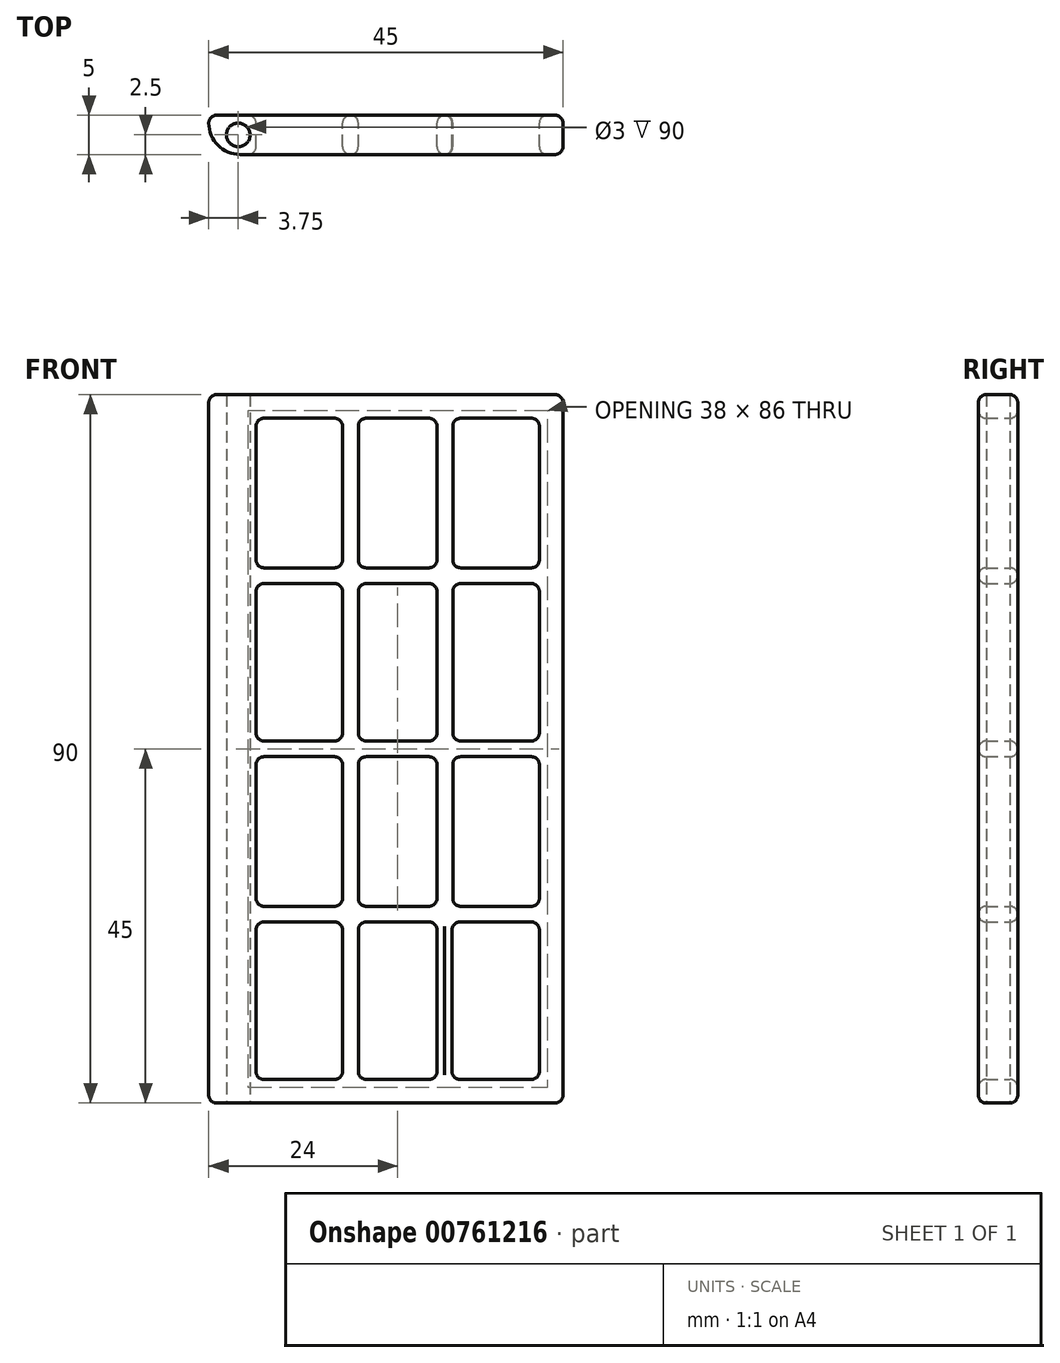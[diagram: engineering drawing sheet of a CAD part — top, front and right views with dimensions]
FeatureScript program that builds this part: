
annotation { "Feature Type Name" : "Feature", "Feature Type Description" : "" }
export const myFeature = defineFeature(function(context is Context, id is Id, definition is map)
    precondition{}
    {
        {
            var Q0;
            Q0=qCreatedBy(makeId("Front.planeOp"),FACE);
            var sketch = newSketch(context, id + "F0", { "sketchPlane" : qUnion([Q0])});
            skLineSegment(sketch, "E0.bottom", {"start": v(0, 0) * mm, "end": v(45, 0) * mm});
            skLineSegment(sketch, "E0.top", {"start": v(0, 90) * mm, "end": v(45, 90) * mm});
            skLineSegment(sketch, "E0.left", {"start": v(0, 0) * mm, "end": v(0, 90) * mm});
            skLineSegment(sketch, "E0.right", {"start": v(45, 0) * mm, "end": v(45, 90) * mm});
            skLineSegment(sketch, "E1.bottom", {"start": v(6, 87) * mm, "end": v(17, 87) * mm});
            skLineSegment(sketch, "E1.top", {"start": v(6, 68) * mm, "end": v(17, 68) * mm});
            skLineSegment(sketch, "E1.left", {"start": v(6, 87) * mm, "end": v(6, 68) * mm});
            skLineSegment(sketch, "E1.right", {"start": v(17, 87) * mm, "end": v(17, 68) * mm});
            skLineSegment(sketch, "E2.bottom", {"start": v(19, 87) * mm, "end": v(29, 87) * mm});
            skLineSegment(sketch, "E2.top", {"start": v(19, 68) * mm, "end": v(29, 68) * mm});
            skLineSegment(sketch, "E2.left", {"start": v(19, 87) * mm, "end": v(19, 68) * mm});
            skLineSegment(sketch, "E2.right", {"start": v(29, 87) * mm, "end": v(29, 68) * mm});
            skLineSegment(sketch, "E3.bottom", {"start": v(31, 87) * mm, "end": v(42, 87) * mm});
            skLineSegment(sketch, "E3.top", {"start": v(31, 68) * mm, "end": v(42, 68) * mm});
            skLineSegment(sketch, "E3.left", {"start": v(31, 87) * mm, "end": v(31, 68) * mm});
            skLineSegment(sketch, "E3.right", {"start": v(42, 87) * mm, "end": v(42, 68) * mm});
            skLineSegment(sketch, "E4.bottom", {"start": v(6, 66) * mm, "end": v(17, 66) * mm});
            skLineSegment(sketch, "E4.top", {"start": v(6, 46) * mm, "end": v(17, 46) * mm});
            skLineSegment(sketch, "E4.left", {"start": v(6, 66) * mm, "end": v(6, 46) * mm});
            skLineSegment(sketch, "E4.right", {"start": v(17, 66) * mm, "end": v(17, 46) * mm});
            skLineSegment(sketch, "E5.bottom", {"start": v(19, 66) * mm, "end": v(29, 66) * mm});
            skLineSegment(sketch, "E5.top", {"start": v(19, 46) * mm, "end": v(29, 46) * mm});
            skLineSegment(sketch, "E5.left", {"start": v(19, 66) * mm, "end": v(19, 46) * mm});
            skLineSegment(sketch, "E5.right", {"start": v(29, 66) * mm, "end": v(29, 46) * mm});
            skLineSegment(sketch, "E6.bottom", {"start": v(31, 66) * mm, "end": v(42, 66) * mm});
            skLineSegment(sketch, "E6.top", {"start": v(31, 46) * mm, "end": v(42, 46) * mm});
            skLineSegment(sketch, "E6.left", {"start": v(31, 66) * mm, "end": v(31, 46) * mm});
            skLineSegment(sketch, "E6.right", {"start": v(42, 66) * mm, "end": v(42, 46) * mm});
            skLineSegment(sketch, "E7.bottom", {"start": v(6, 44) * mm, "end": v(17, 44) * mm});
            skLineSegment(sketch, "E7.top", {"start": v(6, 25) * mm, "end": v(17, 25) * mm});
            skLineSegment(sketch, "E7.left", {"start": v(6, 44) * mm, "end": v(6, 25) * mm});
            skLineSegment(sketch, "E7.right", {"start": v(17, 44) * mm, "end": v(17, 25) * mm});
            skLineSegment(sketch, "E8.bottom", {"start": v(19, 44) * mm, "end": v(29, 44) * mm});
            skLineSegment(sketch, "E8.top", {"start": v(19, 25) * mm, "end": v(29, 25) * mm});
            skLineSegment(sketch, "E8.left", {"start": v(19, 44) * mm, "end": v(19, 25) * mm});
            skLineSegment(sketch, "E8.right", {"start": v(29, 44) * mm, "end": v(29, 25) * mm});
            skLineSegment(sketch, "E9.bottom", {"start": v(31, 44) * mm, "end": v(42, 44) * mm});
            skLineSegment(sketch, "E9.top", {"start": v(31, 25) * mm, "end": v(42, 25) * mm});
            skLineSegment(sketch, "E9.left", {"start": v(31, 44) * mm, "end": v(31, 25) * mm});
            skLineSegment(sketch, "E9.right", {"start": v(42, 44) * mm, "end": v(42, 25) * mm});
            skLineSegment(sketch, "E10.bottom", {"start": v(6, 23) * mm, "end": v(17, 23) * mm});
            skLineSegment(sketch, "E10.top", {"start": v(6, 3) * mm, "end": v(17, 3) * mm});
            skLineSegment(sketch, "E10.left", {"start": v(6, 23) * mm, "end": v(6, 3) * mm});
            skLineSegment(sketch, "E10.right", {"start": v(17, 23) * mm, "end": v(17, 3) * mm});
            skLineSegment(sketch, "E11.bottom", {"start": v(19, 23) * mm, "end": v(29, 23) * mm});
            skLineSegment(sketch, "E11.top", {"start": v(19, 3) * mm, "end": v(29, 3) * mm});
            skLineSegment(sketch, "E11.left", {"start": v(19, 23) * mm, "end": v(19, 3) * mm});
            skLineSegment(sketch, "E11.right", {"start": v(29, 23) * mm, "end": v(29, 3) * mm});
            skLineSegment(sketch, "E12.bottom", {"start": v(30.9, 23) * mm, "end": v(42, 23) * mm});
            skLineSegment(sketch, "E12.left", {"start": v(30.9, 23) * mm, "end": v(30.9, 3) * mm});
            skLineSegment(sketch, "E12.right", {"start": v(42, 23) * mm, "end": v(42, 3) * mm});
            skLineSegment(sketch, "E13", {"start": v(30.9, 3) * mm, "end": v(42, 3) * mm});
            skSolve(sketch);
        }
        {
            var Q0;
            Q0=makeQuery(id+"F0.imprint","IMPRINT",FACE,{"disambiguationData":[TD([[makeQuery(id+"F0.imprint","IMPRINT",EDGE,{"derivedFrom":sQuery(id+"F0.wireOp",EDGE,"E0.bottom")}),1.0]])]});
            extrude(context, id + "F1", {"entities" : qUnion([Q0]), "depth" : 5 * mm, "offsetDistance" : 25 * mm});
        }
        {
            var Q0;
            Q0=qCreatedBy(makeId("Top.planeOp"),FACE);
            var sketch = newSketch(context, id + "F2", { "sketchPlane" : qUnion([Q0])});
            skPoint(sketch, "E14", {"position": v(3.75, -2.5) * mm});
            skSolve(sketch);
        }
        {
            var Q0;
            Q0=sQuery(id+"F2.wireOp",VERTEX,"E14");
            var Q1;
            Q1=makeQuery(id+"F1.opExtrude","SWEPT_BODY",BODY,{"disambiguationData":[OSD([sQuery(id+"F0.wireOp",EDGE,"E0.bottom"),sQuery(id+"F0.wireOp",EDGE,"E0.top"),sQuery(id+"F0.wireOp",EDGE,"E0.left"),sQuery(id+"F0.wireOp",EDGE,"E0.right"),sQuery(id+"F0.wireOp",EDGE,"E1.bottom"),sQuery(id+"F0.wireOp",EDGE,"E1.top"),sQuery(id+"F0.wireOp",EDGE,"E1.left"),sQuery(id+"F0.wireOp",EDGE,"E1.right"),sQuery(id+"F0.wireOp",EDGE,"E2.bottom"),sQuery(id+"F0.wireOp",EDGE,"E2.top"),sQuery(id+"F0.wireOp",EDGE,"E2.left"),sQuery(id+"F0.wireOp",EDGE,"E2.right"),sQuery(id+"F0.wireOp",EDGE,"E3.bottom"),sQuery(id+"F0.wireOp",EDGE,"E3.top"),sQuery(id+"F0.wireOp",EDGE,"E3.left"),sQuery(id+"F0.wireOp",EDGE,"E3.right"),sQuery(id+"F0.wireOp",EDGE,"E4.bottom"),sQuery(id+"F0.wireOp",EDGE,"E4.top"),sQuery(id+"F0.wireOp",EDGE,"E4.left"),sQuery(id+"F0.wireOp",EDGE,"E4.right"),sQuery(id+"F0.wireOp",EDGE,"E5.bottom"),sQuery(id+"F0.wireOp",EDGE,"E5.top"),sQuery(id+"F0.wireOp",EDGE,"E5.left"),sQuery(id+"F0.wireOp",EDGE,"E5.right"),sQuery(id+"F0.wireOp",EDGE,"E6.bottom"),sQuery(id+"F0.wireOp",EDGE,"E6.top"),sQuery(id+"F0.wireOp",EDGE,"E6.left"),sQuery(id+"F0.wireOp",EDGE,"E6.right"),sQuery(id+"F0.wireOp",EDGE,"E7.bottom"),sQuery(id+"F0.wireOp",EDGE,"E7.top"),sQuery(id+"F0.wireOp",EDGE,"E7.left"),sQuery(id+"F0.wireOp",EDGE,"E7.right"),sQuery(id+"F0.wireOp",EDGE,"E8.bottom"),sQuery(id+"F0.wireOp",EDGE,"E8.top"),sQuery(id+"F0.wireOp",EDGE,"E8.left"),sQuery(id+"F0.wireOp",EDGE,"E8.right"),sQuery(id+"F0.wireOp",EDGE,"E9.bottom"),sQuery(id+"F0.wireOp",EDGE,"E9.top"),sQuery(id+"F0.wireOp",EDGE,"E9.left"),sQuery(id+"F0.wireOp",EDGE,"E9.right"),sQuery(id+"F0.wireOp",EDGE,"E10.bottom"),sQuery(id+"F0.wireOp",EDGE,"E10.top"),sQuery(id+"F0.wireOp",EDGE,"E10.left"),sQuery(id+"F0.wireOp",EDGE,"E10.right"),sQuery(id+"F0.wireOp",EDGE,"E11.bottom"),sQuery(id+"F0.wireOp",EDGE,"E11.top"),sQuery(id+"F0.wireOp",EDGE,"E11.left"),sQuery(id+"F0.wireOp",EDGE,"E11.right"),sQuery(id+"F0.wireOp",EDGE,"E12.bottom"),sQuery(id+"F0.wireOp",EDGE,"E12.left"),sQuery(id+"F0.wireOp",EDGE,"E12.right"),sQuery(id+"F0.wireOp",EDGE,"E13")])]});
            hole(context, id + "F3", {"style" : HoleStyle.SIMPLE, "endStyle" : HoleEndStyle.BLIND, "oppositeDirection" : true, "holeDiameter" : 3 * mm, "majorDiameter" : 5 * mm, "holeDepth" : 150 * mm, "isTappedThrough" : true, "tappedDepth" : 12 * mm, "tapClearance" : 3, "locations" : qUnion([Q0]), "scope" : qUnion([Q1])});
        }
        {
            var Q0;
            Q0=makeQuery(id+"F1.opExtrude","CAP_EDGE",EDGE,{"disambiguationData":[OSD([sQuery(id+"F0.wireOp",EDGE,"E0.left")])],"isStart":false});
            fillet(context, id + "F4", {"entities" : qUnion([Q0]), "radius" : 4 * mm, "tangentPropagation" : true, "allowEdgeOverflow" : false});
        }
        {
            var Q0;
            Q0=makeQuery(id+"F1.opExtrude","CAP_EDGE",EDGE,{"disambiguationData":[OSD([sQuery(id+"F0.wireOp",EDGE,"E1.left")])],"isStart":false});
            var Q1;
            Q1=makeQuery(id+"F1.opExtrude","CAP_EDGE",EDGE,{"disambiguationData":[OSD([sQuery(id+"F0.wireOp",EDGE,"E1.bottom")])],"isStart":false});
            var Q2;
            Q2=makeQuery(id+"F1.opExtrude","CAP_EDGE",EDGE,{"disambiguationData":[OSD([sQuery(id+"F0.wireOp",EDGE,"E1.right")])],"isStart":false});
            var Q3;
            Q3=makeQuery(id+"F1.opExtrude","CAP_EDGE",EDGE,{"disambiguationData":[OSD([sQuery(id+"F0.wireOp",EDGE,"E1.top")])],"isStart":false});
            var Q4;
            Q4=makeQuery(id+"F1.opExtrude","CAP_EDGE",EDGE,{"disambiguationData":[OSD([sQuery(id+"F0.wireOp",EDGE,"E2.left")])],"isStart":false});
            var Q5;
            Q5=makeQuery(id+"F1.opExtrude","CAP_EDGE",EDGE,{"disambiguationData":[OSD([sQuery(id+"F0.wireOp",EDGE,"E2.bottom")])],"isStart":false});
            var Q6;
            Q6=makeQuery(id+"F1.opExtrude","CAP_EDGE",EDGE,{"disambiguationData":[OSD([sQuery(id+"F0.wireOp",EDGE,"E2.right")])],"isStart":false});
            var Q7;
            Q7=makeQuery(id+"F1.opExtrude","CAP_EDGE",EDGE,{"disambiguationData":[OSD([sQuery(id+"F0.wireOp",EDGE,"E2.top")])],"isStart":false});
            var Q8;
            Q8=makeQuery(id+"F1.opExtrude","CAP_EDGE",EDGE,{"disambiguationData":[OSD([sQuery(id+"F0.wireOp",EDGE,"E3.left")])],"isStart":false});
            var Q9;
            Q9=makeQuery(id+"F1.opExtrude","CAP_EDGE",EDGE,{"disambiguationData":[OSD([sQuery(id+"F0.wireOp",EDGE,"E3.bottom")])],"isStart":false});
            var Q10;
            Q10=makeQuery(id+"F1.opExtrude","CAP_EDGE",EDGE,{"disambiguationData":[OSD([sQuery(id+"F0.wireOp",EDGE,"E3.right")])],"isStart":false});
            var Q11;
            Q11=makeQuery(id+"F1.opExtrude","CAP_EDGE",EDGE,{"disambiguationData":[OSD([sQuery(id+"F0.wireOp",EDGE,"E3.top")])],"isStart":false});
            var Q12;
            Q12=makeQuery(id+"F1.opExtrude","CAP_EDGE",EDGE,{"disambiguationData":[OSD([sQuery(id+"F0.wireOp",EDGE,"E4.left")])],"isStart":false});
            var Q13;
            Q13=makeQuery(id+"F1.opExtrude","CAP_EDGE",EDGE,{"disambiguationData":[OSD([sQuery(id+"F0.wireOp",EDGE,"E4.bottom")])],"isStart":false});
            var Q14;
            Q14=makeQuery(id+"F1.opExtrude","CAP_EDGE",EDGE,{"disambiguationData":[OSD([sQuery(id+"F0.wireOp",EDGE,"E4.right")])],"isStart":false});
            var Q15;
            Q15=makeQuery(id+"F1.opExtrude","CAP_EDGE",EDGE,{"disambiguationData":[OSD([sQuery(id+"F0.wireOp",EDGE,"E13")])],"isStart":false});
            var Q16;
            Q16=makeQuery(id+"F1.opExtrude","CAP_EDGE",EDGE,{"disambiguationData":[OSD([sQuery(id+"F0.wireOp",EDGE,"E0.bottom")])],"isStart":false});
            var Q17;
            Q17=makeQuery(id+"F1.opExtrude","CAP_EDGE",EDGE,{"disambiguationData":[OSD([sQuery(id+"F0.wireOp",EDGE,"E12.bottom")])],"isStart":false});
            var Q18;
            Q18=makeQuery(id+"F1.opExtrude","CAP_EDGE",EDGE,{"disambiguationData":[OSD([sQuery(id+"F0.wireOp",EDGE,"E8.top")])],"isStart":false});
            var Q19;
            Q19=makeQuery(id+"F1.opExtrude","CAP_EDGE",EDGE,{"disambiguationData":[OSD([sQuery(id+"F0.wireOp",EDGE,"E4.top")])],"isStart":false});
            var Q20;
            Q20=makeQuery(id+"F1.opExtrude","CAP_EDGE",EDGE,{"disambiguationData":[OSD([sQuery(id+"F0.wireOp",EDGE,"E12.right")])],"isStart":false});
            var Q21;
            Q21=makeQuery(id+"F1.opExtrude","CAP_EDGE",EDGE,{"disambiguationData":[OSD([sQuery(id+"F0.wireOp",EDGE,"E6.right")])],"isStart":false});
            var Q22;
            Q22=makeQuery(id+"F1.opExtrude","CAP_EDGE",EDGE,{"disambiguationData":[OSD([sQuery(id+"F0.wireOp",EDGE,"E8.right")])],"isStart":false});
            var Q23;
            Q23=makeQuery(id+"F1.opExtrude","CAP_EDGE",EDGE,{"disambiguationData":[OSD([sQuery(id+"F0.wireOp",EDGE,"E10.left")])],"isStart":false});
            var Q24;
            Q24=makeQuery(id+"F1.opExtrude","CAP_EDGE",EDGE,{"disambiguationData":[OSD([sQuery(id+"F0.wireOp",EDGE,"E6.left")])],"isStart":false});
            var Q25;
            Q25=makeQuery(id+"F1.opExtrude","CAP_EDGE",EDGE,{"disambiguationData":[OSD([sQuery(id+"F0.wireOp",EDGE,"E8.bottom")])],"isStart":false});
            var Q26;
            Q26=makeQuery(id+"F1.opExtrude","CAP_EDGE",EDGE,{"disambiguationData":[OSD([sQuery(id+"F0.wireOp",EDGE,"E0.right")])],"isStart":true});
            var Q27;
            Q27=makeQuery(id+"F1.opExtrude","CAP_EDGE",EDGE,{"disambiguationData":[OSD([sQuery(id+"F0.wireOp",EDGE,"E0.top")])],"isStart":true});
            var Q28;
            Q28=makeQuery(id+"F1.opExtrude","CAP_EDGE",EDGE,{"disambiguationData":[OSD([sQuery(id+"F0.wireOp",EDGE,"E6.bottom")])],"isStart":false});
            var Q29;
            Q29=makeQuery(id+"F1.opExtrude","CAP_EDGE",EDGE,{"disambiguationData":[OSD([sQuery(id+"F0.wireOp",EDGE,"E10.right")])],"isStart":false});
            var Q30;
            Q30=makeQuery(id+"F1.opExtrude","CAP_EDGE",EDGE,{"disambiguationData":[OSD([sQuery(id+"F0.wireOp",EDGE,"E10.top")])],"isStart":false});
            var Q31;
            {var subQ0=sQuery(id+"F0.wireOp",EDGE,"E0.left");Q31=makeQuery(id+"F4.opFillet","BLEND_EDGE",EDGE,{"blendedFrom":[makeQuery(id+"F1.opExtrude","CAP_EDGE",EDGE,{"disambiguationData":[OSD([subQ0])],"isStart":false}),makeQuery(id+"F1.opExtrude","CAP_FACE",FACE,{"disambiguationData":[OSD([sQuery(id+"F0.wireOp",EDGE,"E0.bottom"),sQuery(id+"F0.wireOp",EDGE,"E0.top"),subQ0,sQuery(id+"F0.wireOp",EDGE,"E0.right"),sQuery(id+"F0.wireOp",EDGE,"E1.bottom"),sQuery(id+"F0.wireOp",EDGE,"E1.top"),sQuery(id+"F0.wireOp",EDGE,"E1.left"),sQuery(id+"F0.wireOp",EDGE,"E1.right"),sQuery(id+"F0.wireOp",EDGE,"E2.bottom"),sQuery(id+"F0.wireOp",EDGE,"E2.top"),sQuery(id+"F0.wireOp",EDGE,"E2.left"),sQuery(id+"F0.wireOp",EDGE,"E2.right"),sQuery(id+"F0.wireOp",EDGE,"E3.bottom"),sQuery(id+"F0.wireOp",EDGE,"E3.top"),sQuery(id+"F0.wireOp",EDGE,"E3.left"),sQuery(id+"F0.wireOp",EDGE,"E3.right"),sQuery(id+"F0.wireOp",EDGE,"E4.bottom"),sQuery(id+"F0.wireOp",EDGE,"E4.top"),sQuery(id+"F0.wireOp",EDGE,"E4.left"),sQuery(id+"F0.wireOp",EDGE,"E4.right"),sQuery(id+"F0.wireOp",EDGE,"E5.bottom"),sQuery(id+"F0.wireOp",EDGE,"E5.top"),sQuery(id+"F0.wireOp",EDGE,"E5.left"),sQuery(id+"F0.wireOp",EDGE,"E5.right"),sQuery(id+"F0.wireOp",EDGE,"E6.bottom"),sQuery(id+"F0.wireOp",EDGE,"E6.top"),sQuery(id+"F0.wireOp",EDGE,"E6.left"),sQuery(id+"F0.wireOp",EDGE,"E6.right"),sQuery(id+"F0.wireOp",EDGE,"E7.bottom"),sQuery(id+"F0.wireOp",EDGE,"E7.top"),sQuery(id+"F0.wireOp",EDGE,"E7.left"),sQuery(id+"F0.wireOp",EDGE,"E7.right"),sQuery(id+"F0.wireOp",EDGE,"E8.bottom"),sQuery(id+"F0.wireOp",EDGE,"E8.top"),sQuery(id+"F0.wireOp",EDGE,"E8.left"),sQuery(id+"F0.wireOp",EDGE,"E8.right"),sQuery(id+"F0.wireOp",EDGE,"E9.bottom"),sQuery(id+"F0.wireOp",EDGE,"E9.top"),sQuery(id+"F0.wireOp",EDGE,"E9.left"),sQuery(id+"F0.wireOp",EDGE,"E9.right"),sQuery(id+"F0.wireOp",EDGE,"E10.bottom"),sQuery(id+"F0.wireOp",EDGE,"E10.top"),sQuery(id+"F0.wireOp",EDGE,"E10.left"),sQuery(id+"F0.wireOp",EDGE,"E10.right"),sQuery(id+"F0.wireOp",EDGE,"E11.bottom"),sQuery(id+"F0.wireOp",EDGE,"E11.top"),sQuery(id+"F0.wireOp",EDGE,"E11.left"),sQuery(id+"F0.wireOp",EDGE,"E11.right"),sQuery(id+"F0.wireOp",EDGE,"E12.bottom"),sQuery(id+"F0.wireOp",EDGE,"E12.left"),sQuery(id+"F0.wireOp",EDGE,"E12.right"),sQuery(id+"F0.wireOp",EDGE,"E13")])],"isStart":false})],"blendedInto":[makeQuery(id+"F1.opExtrude","CAP_FACE",FACE,{"disambiguationData":[OSD([sQuery(id+"F0.wireOp",EDGE,"E0.bottom"),sQuery(id+"F0.wireOp",EDGE,"E0.top"),subQ0,sQuery(id+"F0.wireOp",EDGE,"E0.right"),sQuery(id+"F0.wireOp",EDGE,"E1.bottom"),sQuery(id+"F0.wireOp",EDGE,"E1.top"),sQuery(id+"F0.wireOp",EDGE,"E1.left"),sQuery(id+"F0.wireOp",EDGE,"E1.right"),sQuery(id+"F0.wireOp",EDGE,"E2.bottom"),sQuery(id+"F0.wireOp",EDGE,"E2.top"),sQuery(id+"F0.wireOp",EDGE,"E2.left"),sQuery(id+"F0.wireOp",EDGE,"E2.right"),sQuery(id+"F0.wireOp",EDGE,"E3.bottom"),sQuery(id+"F0.wireOp",EDGE,"E3.top"),sQuery(id+"F0.wireOp",EDGE,"E3.left"),sQuery(id+"F0.wireOp",EDGE,"E3.right"),sQuery(id+"F0.wireOp",EDGE,"E4.bottom"),sQuery(id+"F0.wireOp",EDGE,"E4.top"),sQuery(id+"F0.wireOp",EDGE,"E4.left"),sQuery(id+"F0.wireOp",EDGE,"E4.right"),sQuery(id+"F0.wireOp",EDGE,"E5.bottom"),sQuery(id+"F0.wireOp",EDGE,"E5.top"),sQuery(id+"F0.wireOp",EDGE,"E5.left"),sQuery(id+"F0.wireOp",EDGE,"E5.right"),sQuery(id+"F0.wireOp",EDGE,"E6.bottom"),sQuery(id+"F0.wireOp",EDGE,"E6.top"),sQuery(id+"F0.wireOp",EDGE,"E6.left"),sQuery(id+"F0.wireOp",EDGE,"E6.right"),sQuery(id+"F0.wireOp",EDGE,"E7.bottom"),sQuery(id+"F0.wireOp",EDGE,"E7.top"),sQuery(id+"F0.wireOp",EDGE,"E7.left"),sQuery(id+"F0.wireOp",EDGE,"E7.right"),sQuery(id+"F0.wireOp",EDGE,"E8.bottom"),sQuery(id+"F0.wireOp",EDGE,"E8.top"),sQuery(id+"F0.wireOp",EDGE,"E8.left"),sQuery(id+"F0.wireOp",EDGE,"E8.right"),sQuery(id+"F0.wireOp",EDGE,"E9.bottom"),sQuery(id+"F0.wireOp",EDGE,"E9.top"),sQuery(id+"F0.wireOp",EDGE,"E9.left"),sQuery(id+"F0.wireOp",EDGE,"E9.right"),sQuery(id+"F0.wireOp",EDGE,"E10.bottom"),sQuery(id+"F0.wireOp",EDGE,"E10.top"),sQuery(id+"F0.wireOp",EDGE,"E10.left"),sQuery(id+"F0.wireOp",EDGE,"E10.right"),sQuery(id+"F0.wireOp",EDGE,"E11.bottom"),sQuery(id+"F0.wireOp",EDGE,"E11.top"),sQuery(id+"F0.wireOp",EDGE,"E11.left"),sQuery(id+"F0.wireOp",EDGE,"E11.right"),sQuery(id+"F0.wireOp",EDGE,"E12.bottom"),sQuery(id+"F0.wireOp",EDGE,"E12.left"),sQuery(id+"F0.wireOp",EDGE,"E12.right"),sQuery(id+"F0.wireOp",EDGE,"E13")])],"isStart":false})]});}
            var Q32;
            Q32=makeQuery(id+"F1.opExtrude","CAP_EDGE",EDGE,{"disambiguationData":[OSD([sQuery(id+"F0.wireOp",EDGE,"E8.left")])],"isStart":false});
            var Q33;
            Q33=makeQuery(id+"F1.opExtrude","CAP_EDGE",EDGE,{"disambiguationData":[OSD([sQuery(id+"F0.wireOp",EDGE,"E10.bottom")])],"isStart":false});
            var Q34;
            Q34=makeQuery(id+"F4.opFillet","BLEND_EDGE",EDGE,{"blendedFrom":[makeQuery(id+"F1.opExtrude","CAP_EDGE",EDGE,{"disambiguationData":[OSD([sQuery(id+"F0.wireOp",EDGE,"E0.left")])],"isStart":false}),makeQuery(id+"F1.opExtrude","SWEPT_FACE",FACE,{"disambiguationData":[OSD([sQuery(id+"F0.wireOp",EDGE,"E0.top")])]})],"blendedInto":[makeQuery(id+"F1.opExtrude","SWEPT_FACE",FACE,{"disambiguationData":[OSD([sQuery(id+"F0.wireOp",EDGE,"E0.top")])]})]});
            var Q35;
            Q35=makeQuery(id+"F1.opExtrude","CAP_EDGE",EDGE,{"disambiguationData":[OSD([sQuery(id+"F0.wireOp",EDGE,"E12.left")])],"isStart":false});
            var Q36;
            Q36=makeQuery(id+"F1.opExtrude","CAP_EDGE",EDGE,{"disambiguationData":[OSD([sQuery(id+"F0.wireOp",EDGE,"E6.top")])],"isStart":false});
            var Q37;
            Q37=makeQuery(id+"F1.opExtrude","CAP_EDGE",EDGE,{"disambiguationData":[OSD([sQuery(id+"F0.wireOp",EDGE,"E11.right")])],"isStart":false});
            var Q38;
            Q38=makeQuery(id+"F1.opExtrude","CAP_EDGE",EDGE,{"disambiguationData":[OSD([sQuery(id+"F0.wireOp",EDGE,"E9.right")])],"isStart":false});
            var Q39;
            Q39=makeQuery(id+"F1.opExtrude","CAP_EDGE",EDGE,{"disambiguationData":[OSD([sQuery(id+"F0.wireOp",EDGE,"E7.right")])],"isStart":false});
            var Q40;
            Q40=makeQuery(id+"F1.opExtrude","CAP_EDGE",EDGE,{"disambiguationData":[OSD([sQuery(id+"F0.wireOp",EDGE,"E5.right")])],"isStart":false});
            var Q41;
            Q41=makeQuery(id+"F1.opExtrude","SWEPT_EDGE",EDGE,{"disambiguationData":[OSD([sQuery(id+"F0.wireOp",EDGE,"E8.top"),sQuery(id+"F0.wireOp",EDGE,"E8.right")])]});
            var Q42;
            Q42=makeQuery(id+"F1.opExtrude","SWEPT_EDGE",EDGE,{"disambiguationData":[OSD([sQuery(id+"F0.wireOp",EDGE,"E8.top"),sQuery(id+"F0.wireOp",EDGE,"E8.left")])]});
            var Q43;
            Q43=makeQuery(id+"F1.opExtrude","CAP_EDGE",EDGE,{"disambiguationData":[OSD([sQuery(id+"F0.wireOp",EDGE,"E9.left")])],"isStart":false});
            var Q44;
            Q44=makeQuery(id+"F1.opExtrude","CAP_EDGE",EDGE,{"disambiguationData":[OSD([sQuery(id+"F0.wireOp",EDGE,"E11.left")])],"isStart":false});
            var Q45;
            Q45=makeQuery(id+"F1.opExtrude","CAP_EDGE",EDGE,{"disambiguationData":[OSD([sQuery(id+"F0.wireOp",EDGE,"E5.left")])],"isStart":false});
            var Q46;
            Q46=makeQuery(id+"F1.opExtrude","CAP_EDGE",EDGE,{"disambiguationData":[OSD([sQuery(id+"F0.wireOp",EDGE,"E7.left")])],"isStart":false});
            var Q47;
            Q47=makeQuery(id+"F1.opExtrude","SWEPT_EDGE",EDGE,{"disambiguationData":[OSD([sQuery(id+"F0.wireOp",EDGE,"E12.bottom"),sQuery(id+"F0.wireOp",EDGE,"E12.right")])]});
            var Q48;
            Q48=makeQuery(id+"F1.opExtrude","SWEPT_EDGE",EDGE,{"disambiguationData":[OSD([sQuery(id+"F0.wireOp",EDGE,"E12.bottom"),sQuery(id+"F0.wireOp",EDGE,"E12.left")])]});
            var Q49;
            Q49=makeQuery(id+"F1.opExtrude","CAP_EDGE",EDGE,{"disambiguationData":[OSD([sQuery(id+"F0.wireOp",EDGE,"E11.top")])],"isStart":false});
            var Q50;
            Q50=makeQuery(id+"F1.opExtrude","CAP_EDGE",EDGE,{"disambiguationData":[OSD([sQuery(id+"F0.wireOp",EDGE,"E7.top")])],"isStart":false});
            var Q51;
            Q51=makeQuery(id+"F1.opExtrude","CAP_EDGE",EDGE,{"disambiguationData":[OSD([sQuery(id+"F0.wireOp",EDGE,"E9.top")])],"isStart":false});
            var Q52;
            Q52=makeQuery(id+"F1.opExtrude","CAP_EDGE",EDGE,{"disambiguationData":[OSD([sQuery(id+"F0.wireOp",EDGE,"E5.top")])],"isStart":false});
            var Q53;
            Q53=makeQuery(id+"F1.opExtrude","SWEPT_EDGE",EDGE,{"disambiguationData":[OSD([sQuery(id+"F0.wireOp",EDGE,"E7.top"),sQuery(id+"F0.wireOp",EDGE,"E7.right")])]});
            var Q54;
            Q54=makeQuery(id+"F1.opExtrude","CAP_EDGE",EDGE,{"disambiguationData":[OSD([sQuery(id+"F0.wireOp",EDGE,"E11.bottom")])],"isStart":false});
            var Q55;
            Q55=makeQuery(id+"F1.opExtrude","CAP_EDGE",EDGE,{"disambiguationData":[OSD([sQuery(id+"F0.wireOp",EDGE,"E9.bottom")])],"isStart":false});
            var Q56;
            Q56=makeQuery(id+"F1.opExtrude","CAP_EDGE",EDGE,{"disambiguationData":[OSD([sQuery(id+"F0.wireOp",EDGE,"E7.bottom")])],"isStart":false});
            var Q57;
            Q57=makeQuery(id+"F1.opExtrude","CAP_EDGE",EDGE,{"disambiguationData":[OSD([sQuery(id+"F0.wireOp",EDGE,"E5.bottom")])],"isStart":false});
            var Q58;
            Q58=makeQuery(id+"F1.opExtrude","SWEPT_EDGE",EDGE,{"disambiguationData":[OSD([sQuery(id+"F0.wireOp",EDGE,"E11.bottom"),sQuery(id+"F0.wireOp",EDGE,"E11.right")])]});
            var Q59;
            {var subQ0=sQuery(id+"F0.wireOp",EDGE,"E0.left");Q59=makeQuery(id+"F4.opFillet","BLEND_EDGE",EDGE,{"blendedFrom":[makeQuery(id+"F1.opExtrude","CAP_EDGE",EDGE,{"disambiguationData":[OSD([subQ0])],"isStart":false}),makeQuery(id+"F1.opExtrude","SWEPT_FACE",FACE,{"disambiguationData":[OSD([subQ0])]})],"blendedInto":[makeQuery(id+"F1.opExtrude","SWEPT_FACE",FACE,{"disambiguationData":[OSD([subQ0])]})]});}
            var Q60;
            Q60=makeQuery(id+"F1.opExtrude","SWEPT_EDGE",EDGE,{"disambiguationData":[OSD([sQuery(id+"F0.wireOp",EDGE,"E0.bottom"),sQuery(id+"F0.wireOp",EDGE,"E0.right")])]});
            var Q61;
            Q61=makeQuery(id+"F1.opExtrude","CAP_EDGE",EDGE,{"disambiguationData":[OSD([sQuery(id+"F0.wireOp",EDGE,"E0.bottom")])],"isStart":true});
            var Q62;
            Q62=makeQuery(id+"F1.opExtrude","CAP_EDGE",EDGE,{"disambiguationData":[OSD([sQuery(id+"F0.wireOp",EDGE,"E8.bottom")])],"isStart":true});
            var Q63;
            Q63=makeQuery(id+"F1.opExtrude","CAP_EDGE",EDGE,{"disambiguationData":[OSD([sQuery(id+"F0.wireOp",EDGE,"E6.left")])],"isStart":true});
            var Q64;
            Q64=makeQuery(id+"F1.opExtrude","SWEPT_EDGE",EDGE,{"disambiguationData":[OSD([sQuery(id+"F0.wireOp",EDGE,"E10.bottom"),sQuery(id+"F0.wireOp",EDGE,"E10.left")])]});
            var Q65;
            Q65=makeQuery(id+"F1.opExtrude","SWEPT_EDGE",EDGE,{"disambiguationData":[OSD([sQuery(id+"F0.wireOp",EDGE,"E10.top"),sQuery(id+"F0.wireOp",EDGE,"E10.left")])]});
            var Q66;
            Q66=makeQuery(id+"F1.opExtrude","CAP_EDGE",EDGE,{"disambiguationData":[OSD([sQuery(id+"F0.wireOp",EDGE,"E9.bottom")])],"isStart":true});
            var Q67;
            Q67=makeQuery(id+"F1.opExtrude","SWEPT_EDGE",EDGE,{"disambiguationData":[OSD([sQuery(id+"F0.wireOp",EDGE,"E6.bottom"),sQuery(id+"F0.wireOp",EDGE,"E6.left")])]});
            var Q68;
            Q68=makeQuery(id+"F1.opExtrude","SWEPT_EDGE",EDGE,{"disambiguationData":[OSD([sQuery(id+"F0.wireOp",EDGE,"E5.bottom"),sQuery(id+"F0.wireOp",EDGE,"E5.left")])]});
            var Q69;
            Q69=makeQuery(id+"F1.opExtrude","CAP_EDGE",EDGE,{"disambiguationData":[OSD([sQuery(id+"F0.wireOp",EDGE,"E12.bottom")])],"isStart":true});
            var Q70;
            Q70=makeQuery(id+"F1.opExtrude","SWEPT_EDGE",EDGE,{"disambiguationData":[OSD([sQuery(id+"F0.wireOp",EDGE,"E9.bottom"),sQuery(id+"F0.wireOp",EDGE,"E9.right")])]});
            var Q71;
            Q71=makeQuery(id+"F1.opExtrude","CAP_EDGE",EDGE,{"disambiguationData":[OSD([sQuery(id+"F0.wireOp",EDGE,"E10.left")])],"isStart":true});
            var Q72;
            Q72=makeQuery(id+"F1.opExtrude","SWEPT_EDGE",EDGE,{"disambiguationData":[OSD([sQuery(id+"F0.wireOp",EDGE,"E9.top"),sQuery(id+"F0.wireOp",EDGE,"E9.right")])]});
            var Q73;
            Q73=makeQuery(id+"F1.opExtrude","SWEPT_EDGE",EDGE,{"disambiguationData":[OSD([sQuery(id+"F0.wireOp",EDGE,"E7.bottom"),sQuery(id+"F0.wireOp",EDGE,"E7.left")])]});
            var Q74;
            Q74=makeQuery(id+"F1.opExtrude","CAP_EDGE",EDGE,{"disambiguationData":[OSD([sQuery(id+"F0.wireOp",EDGE,"E2.right")])],"isStart":true});
            var Q75;
            Q75=makeQuery(id+"F1.opExtrude","CAP_EDGE",EDGE,{"disambiguationData":[OSD([sQuery(id+"F0.wireOp",EDGE,"E10.top")])],"isStart":true});
            var Q76;
            Q76=makeQuery(id+"F1.opExtrude","SWEPT_EDGE",EDGE,{"disambiguationData":[OSD([sQuery(id+"F0.wireOp",EDGE,"E10.bottom"),sQuery(id+"F0.wireOp",EDGE,"E10.right")])]});
            var Q77;
            Q77=makeQuery(id+"F1.opExtrude","CAP_EDGE",EDGE,{"disambiguationData":[OSD([sQuery(id+"F0.wireOp",EDGE,"E8.top")])],"isStart":true});
            var Q78;
            Q78=makeQuery(id+"F1.opExtrude","SWEPT_EDGE",EDGE,{"disambiguationData":[OSD([sQuery(id+"F0.wireOp",EDGE,"E6.top"),sQuery(id+"F0.wireOp",EDGE,"E6.left")])]});
            var Q79;
            Q79=makeQuery(id+"F1.opExtrude","SWEPT_EDGE",EDGE,{"disambiguationData":[OSD([sQuery(id+"F0.wireOp",EDGE,"E5.top"),sQuery(id+"F0.wireOp",EDGE,"E5.left")])]});
            var Q80;
            Q80=makeQuery(id+"F1.opExtrude","CAP_EDGE",EDGE,{"disambiguationData":[OSD([sQuery(id+"F0.wireOp",EDGE,"E7.bottom")])],"isStart":true});
            var Q81;
            Q81=makeQuery(id+"F1.opExtrude","CAP_EDGE",EDGE,{"disambiguationData":[OSD([sQuery(id+"F0.wireOp",EDGE,"E4.right")])],"isStart":true});
            var Q82;
            Q82=makeQuery(id+"F1.opExtrude","CAP_EDGE",EDGE,{"disambiguationData":[OSD([sQuery(id+"F0.wireOp",EDGE,"E6.right")])],"isStart":true});
            var Q83;
            Q83=makeQuery(id+"F1.opExtrude","SWEPT_EDGE",EDGE,{"disambiguationData":[OSD([sQuery(id+"F0.wireOp",EDGE,"E5.top"),sQuery(id+"F0.wireOp",EDGE,"E5.right")])]});
            var Q84;
            Q84=makeQuery(id+"F1.opExtrude","SWEPT_EDGE",EDGE,{"disambiguationData":[OSD([sQuery(id+"F0.wireOp",EDGE,"E2.bottom"),sQuery(id+"F0.wireOp",EDGE,"E2.left")])]});
            var Q85;
            Q85=makeQuery(id+"F1.opExtrude","CAP_EDGE",EDGE,{"disambiguationData":[OSD([sQuery(id+"F0.wireOp",EDGE,"E8.right")])],"isStart":true});
            var Q86;
            Q86=makeQuery(id+"F1.opExtrude","CAP_EDGE",EDGE,{"disambiguationData":[OSD([sQuery(id+"F0.wireOp",EDGE,"E4.left")])],"isStart":true});
            var Q87;
            Q87=makeQuery(id+"F1.opExtrude","CAP_EDGE",EDGE,{"disambiguationData":[OSD([sQuery(id+"F0.wireOp",EDGE,"E8.left")])],"isStart":true});
            var Q88;
            Q88=makeQuery(id+"F1.opExtrude","CAP_EDGE",EDGE,{"disambiguationData":[OSD([sQuery(id+"F0.wireOp",EDGE,"E12.right")])],"isStart":true});
            var Q89;
            Q89=makeQuery(id+"F1.opExtrude","CAP_EDGE",EDGE,{"disambiguationData":[OSD([sQuery(id+"F0.wireOp",EDGE,"E6.top")])],"isStart":true});
            var Q90;
            Q90=makeQuery(id+"F1.opExtrude","CAP_EDGE",EDGE,{"disambiguationData":[OSD([sQuery(id+"F0.wireOp",EDGE,"E2.left")])],"isStart":true});
            var Q91;
            Q91=makeQuery(id+"F1.opExtrude","SWEPT_EDGE",EDGE,{"disambiguationData":[OSD([sQuery(id+"F0.wireOp",EDGE,"E9.top"),sQuery(id+"F0.wireOp",EDGE,"E9.left")])]});
            var Q92;
            Q92=makeQuery(id+"F1.opExtrude","CAP_EDGE",EDGE,{"disambiguationData":[OSD([sQuery(id+"F0.wireOp",EDGE,"E3.bottom")])],"isStart":true});
            var Q93;
            Q93=makeQuery(id+"F1.opExtrude","SWEPT_EDGE",EDGE,{"disambiguationData":[OSD([sQuery(id+"F0.wireOp",EDGE,"E11.bottom"),sQuery(id+"F0.wireOp",EDGE,"E11.left")])]});
            var Q94;
            Q94=makeQuery(id+"F1.opExtrude","CAP_EDGE",EDGE,{"disambiguationData":[OSD([sQuery(id+"F0.wireOp",EDGE,"E2.top")])],"isStart":true});
            var Q95;
            Q95=makeQuery(id+"F1.opExtrude","CAP_EDGE",EDGE,{"disambiguationData":[OSD([sQuery(id+"F0.wireOp",EDGE,"E10.right")])],"isStart":true});
            var Q96;
            Q96=makeQuery(id+"F1.opExtrude","SWEPT_EDGE",EDGE,{"disambiguationData":[OSD([sQuery(id+"F0.wireOp",EDGE,"E6.top"),sQuery(id+"F0.wireOp",EDGE,"E6.right")])]});
            var Q97;
            Q97=makeQuery(id+"F1.opExtrude","SWEPT_EDGE",EDGE,{"disambiguationData":[OSD([sQuery(id+"F0.wireOp",EDGE,"E10.top"),sQuery(id+"F0.wireOp",EDGE,"E10.right")])]});
            var Q98;
            Q98=makeQuery(id+"F1.opExtrude","CAP_EDGE",EDGE,{"disambiguationData":[OSD([sQuery(id+"F0.wireOp",EDGE,"E5.bottom")])],"isStart":true});
            var Q99;
            Q99=makeQuery(id+"F1.opExtrude","SWEPT_EDGE",EDGE,{"disambiguationData":[OSD([sQuery(id+"F0.wireOp",EDGE,"E6.bottom"),sQuery(id+"F0.wireOp",EDGE,"E6.right")])]});
            var Q100;
            Q100=makeQuery(id+"F1.opExtrude","CAP_EDGE",EDGE,{"disambiguationData":[OSD([sQuery(id+"F0.wireOp",EDGE,"E12.left")])],"isStart":true});
            var Q101;
            Q101=makeQuery(id+"F1.opExtrude","CAP_EDGE",EDGE,{"disambiguationData":[OSD([sQuery(id+"F0.wireOp",EDGE,"E4.top")])],"isStart":true});
            var Q102;
            Q102=makeQuery(id+"F1.opExtrude","CAP_EDGE",EDGE,{"disambiguationData":[OSD([sQuery(id+"F0.wireOp",EDGE,"E4.bottom")])],"isStart":true});
            var Q103;
            Q103=makeQuery(id+"F1.opExtrude","SWEPT_EDGE",EDGE,{"disambiguationData":[OSD([sQuery(id+"F0.wireOp",EDGE,"E9.bottom"),sQuery(id+"F0.wireOp",EDGE,"E9.left")])]});
            var Q104;
            Q104=makeQuery(id+"F1.opExtrude","CAP_EDGE",EDGE,{"disambiguationData":[OSD([sQuery(id+"F0.wireOp",EDGE,"E2.bottom")])],"isStart":true});
            var Q105;
            Q105=makeQuery(id+"F1.opExtrude","SWEPT_EDGE",EDGE,{"disambiguationData":[OSD([sQuery(id+"F0.wireOp",EDGE,"E5.bottom"),sQuery(id+"F0.wireOp",EDGE,"E5.right")])]});
            var Q106;
            Q106=makeQuery(id+"F1.opExtrude","CAP_EDGE",EDGE,{"disambiguationData":[OSD([sQuery(id+"F0.wireOp",EDGE,"E1.bottom")])],"isStart":true});
            var Q107;
            Q107=makeQuery(id+"F1.opExtrude","CAP_EDGE",EDGE,{"disambiguationData":[OSD([sQuery(id+"F0.wireOp",EDGE,"E11.bottom")])],"isStart":true});
            var Q108;
            Q108=makeQuery(id+"F1.opExtrude","CAP_EDGE",EDGE,{"disambiguationData":[OSD([sQuery(id+"F0.wireOp",EDGE,"E13")])],"isStart":true});
            var Q109;
            Q109=makeQuery(id+"F1.opExtrude","CAP_EDGE",EDGE,{"disambiguationData":[OSD([sQuery(id+"F0.wireOp",EDGE,"E6.bottom")])],"isStart":true});
            var Q110;
            Q110=makeQuery(id+"F1.opExtrude","CAP_EDGE",EDGE,{"disambiguationData":[OSD([sQuery(id+"F0.wireOp",EDGE,"E10.bottom")])],"isStart":true});
            var Q111;
            Q111=makeQuery(id+"F1.opExtrude","SWEPT_EDGE",EDGE,{"disambiguationData":[OSD([sQuery(id+"F0.wireOp",EDGE,"E12.right"),sQuery(id+"F0.wireOp",EDGE,"E13")])]});
            var Q112;
            Q112=makeQuery(id+"F1.opExtrude","SWEPT_EDGE",EDGE,{"disambiguationData":[OSD([sQuery(id+"F0.wireOp",EDGE,"E4.top"),sQuery(id+"F0.wireOp",EDGE,"E4.right")])]});
            var Q113;
            Q113=makeQuery(id+"F1.opExtrude","CAP_EDGE",EDGE,{"disambiguationData":[OSD([sQuery(id+"F0.wireOp",EDGE,"E11.right")])],"isStart":true});
            var Q114;
            Q114=makeQuery(id+"F1.opExtrude","CAP_EDGE",EDGE,{"disambiguationData":[OSD([sQuery(id+"F0.wireOp",EDGE,"E7.right")])],"isStart":true});
            var Q115;
            Q115=makeQuery(id+"F1.opExtrude","CAP_EDGE",EDGE,{"disambiguationData":[OSD([sQuery(id+"F0.wireOp",EDGE,"E9.right")])],"isStart":true});
            var Q116;
            Q116=makeQuery(id+"F1.opExtrude","CAP_EDGE",EDGE,{"disambiguationData":[OSD([sQuery(id+"F0.wireOp",EDGE,"E3.right")])],"isStart":true});
            var Q117;
            Q117=makeQuery(id+"F1.opExtrude","CAP_EDGE",EDGE,{"disambiguationData":[OSD([sQuery(id+"F0.wireOp",EDGE,"E5.right")])],"isStart":true});
            var Q118;
            Q118=makeQuery(id+"F1.opExtrude","CAP_EDGE",EDGE,{"disambiguationData":[OSD([sQuery(id+"F0.wireOp",EDGE,"E1.right")])],"isStart":true});
            var Q119;
            Q119=makeQuery(id+"F1.opExtrude","SWEPT_EDGE",EDGE,{"disambiguationData":[OSD([sQuery(id+"F0.wireOp",EDGE,"E12.left"),sQuery(id+"F0.wireOp",EDGE,"E13")])]});
            var Q120;
            Q120=makeQuery(id+"F1.opExtrude","SWEPT_EDGE",EDGE,{"disambiguationData":[OSD([sQuery(id+"F0.wireOp",EDGE,"E4.top"),sQuery(id+"F0.wireOp",EDGE,"E4.left")])]});
            var Q121;
            Q121=makeQuery(id+"F1.opExtrude","SWEPT_EDGE",EDGE,{"disambiguationData":[OSD([sQuery(id+"F0.wireOp",EDGE,"E4.bottom"),sQuery(id+"F0.wireOp",EDGE,"E4.right")])]});
            var Q122;
            Q122=makeQuery(id+"F1.opExtrude","SWEPT_EDGE",EDGE,{"disambiguationData":[OSD([sQuery(id+"F0.wireOp",EDGE,"E8.bottom"),sQuery(id+"F0.wireOp",EDGE,"E8.right")])]});
            var Q123;
            Q123=makeQuery(id+"F1.opExtrude","CAP_EDGE",EDGE,{"disambiguationData":[OSD([sQuery(id+"F0.wireOp",EDGE,"E9.left")])],"isStart":true});
            var Q124;
            Q124=makeQuery(id+"F1.opExtrude","CAP_EDGE",EDGE,{"disambiguationData":[OSD([sQuery(id+"F0.wireOp",EDGE,"E7.left")])],"isStart":true});
            var Q125;
            Q125=makeQuery(id+"F1.opExtrude","CAP_EDGE",EDGE,{"disambiguationData":[OSD([sQuery(id+"F0.wireOp",EDGE,"E11.left")])],"isStart":true});
            var Q126;
            Q126=makeQuery(id+"F1.opExtrude","CAP_EDGE",EDGE,{"disambiguationData":[OSD([sQuery(id+"F0.wireOp",EDGE,"E3.left")])],"isStart":true});
            var Q127;
            Q127=makeQuery(id+"F1.opExtrude","CAP_EDGE",EDGE,{"disambiguationData":[OSD([sQuery(id+"F0.wireOp",EDGE,"E5.left")])],"isStart":true});
            var Q128;
            Q128=makeQuery(id+"F1.opExtrude","CAP_EDGE",EDGE,{"disambiguationData":[OSD([sQuery(id+"F0.wireOp",EDGE,"E1.left")])],"isStart":true});
            var Q129;
            Q129=makeQuery(id+"F1.opExtrude","SWEPT_EDGE",EDGE,{"disambiguationData":[OSD([sQuery(id+"F0.wireOp",EDGE,"E4.bottom"),sQuery(id+"F0.wireOp",EDGE,"E4.left")])]});
            var Q130;
            Q130=makeQuery(id+"F1.opExtrude","SWEPT_EDGE",EDGE,{"disambiguationData":[OSD([sQuery(id+"F0.wireOp",EDGE,"E8.bottom"),sQuery(id+"F0.wireOp",EDGE,"E8.left")])]});
            var Q131;
            Q131=makeQuery(id+"F1.opExtrude","SWEPT_EDGE",EDGE,{"disambiguationData":[OSD([sQuery(id+"F0.wireOp",EDGE,"E11.top"),sQuery(id+"F0.wireOp",EDGE,"E11.right")])]});
            var Q132;
            Q132=makeQuery(id+"F1.opExtrude","CAP_EDGE",EDGE,{"disambiguationData":[OSD([sQuery(id+"F0.wireOp",EDGE,"E11.top")])],"isStart":true});
            var Q133;
            Q133=makeQuery(id+"F1.opExtrude","CAP_EDGE",EDGE,{"disambiguationData":[OSD([sQuery(id+"F0.wireOp",EDGE,"E9.top")])],"isStart":true});
            var Q134;
            Q134=makeQuery(id+"F1.opExtrude","CAP_EDGE",EDGE,{"disambiguationData":[OSD([sQuery(id+"F0.wireOp",EDGE,"E7.top")])],"isStart":true});
            var Q135;
            Q135=makeQuery(id+"F1.opExtrude","CAP_EDGE",EDGE,{"disambiguationData":[OSD([sQuery(id+"F0.wireOp",EDGE,"E5.top")])],"isStart":true});
            var Q136;
            Q136=makeQuery(id+"F1.opExtrude","CAP_EDGE",EDGE,{"disambiguationData":[OSD([sQuery(id+"F0.wireOp",EDGE,"E3.top")])],"isStart":true});
            var Q137;
            Q137=makeQuery(id+"F1.opExtrude","CAP_EDGE",EDGE,{"disambiguationData":[OSD([sQuery(id+"F0.wireOp",EDGE,"E1.top")])],"isStart":true});
            var Q138;
            Q138=makeQuery(id+"F1.opExtrude","SWEPT_EDGE",EDGE,{"disambiguationData":[OSD([sQuery(id+"F0.wireOp",EDGE,"E11.top"),sQuery(id+"F0.wireOp",EDGE,"E11.left")])]});
            var Q139;
            Q139=makeQuery(id+"F1.opExtrude","SWEPT_EDGE",EDGE,{"disambiguationData":[OSD([sQuery(id+"F0.wireOp",EDGE,"E7.top"),sQuery(id+"F0.wireOp",EDGE,"E7.left")])]});
            var Q140;
            Q140=makeQuery(id+"F1.opExtrude","SWEPT_EDGE",EDGE,{"disambiguationData":[OSD([sQuery(id+"F0.wireOp",EDGE,"E7.bottom"),sQuery(id+"F0.wireOp",EDGE,"E7.right")])]});
            var Q141;
            Q141=makeQuery(id+"F1.opExtrude","SWEPT_EDGE",EDGE,{"disambiguationData":[OSD([sQuery(id+"F0.wireOp",EDGE,"E2.top"),sQuery(id+"F0.wireOp",EDGE,"E2.left")])]});
            var Q142;
            Q142=makeQuery(id+"F1.opExtrude","SWEPT_EDGE",EDGE,{"disambiguationData":[OSD([sQuery(id+"F0.wireOp",EDGE,"E1.top"),sQuery(id+"F0.wireOp",EDGE,"E1.right")])]});
            var Q143;
            Q143=makeQuery(id+"F1.opExtrude","SWEPT_EDGE",EDGE,{"disambiguationData":[OSD([sQuery(id+"F0.wireOp",EDGE,"E2.bottom"),sQuery(id+"F0.wireOp",EDGE,"E2.right")])]});
            var Q144;
            Q144=makeQuery(id+"F1.opExtrude","SWEPT_EDGE",EDGE,{"disambiguationData":[OSD([sQuery(id+"F0.wireOp",EDGE,"E0.top"),sQuery(id+"F0.wireOp",EDGE,"E0.left")])]});
            var Q145;
            Q145=makeQuery(id+"F1.opExtrude","SWEPT_EDGE",EDGE,{"disambiguationData":[OSD([sQuery(id+"F0.wireOp",EDGE,"E1.bottom"),sQuery(id+"F0.wireOp",EDGE,"E1.left")])]});
            var Q146;
            Q146=makeQuery(id+"F1.opExtrude","SWEPT_EDGE",EDGE,{"disambiguationData":[OSD([sQuery(id+"F0.wireOp",EDGE,"E2.top"),sQuery(id+"F0.wireOp",EDGE,"E2.right")])]});
            var Q147;
            Q147=makeQuery(id+"F1.opExtrude","SWEPT_EDGE",EDGE,{"disambiguationData":[OSD([sQuery(id+"F0.wireOp",EDGE,"E3.bottom"),sQuery(id+"F0.wireOp",EDGE,"E3.left")])]});
            var Q148;
            Q148=makeQuery(id+"F1.opExtrude","SWEPT_EDGE",EDGE,{"disambiguationData":[OSD([sQuery(id+"F0.wireOp",EDGE,"E3.top"),sQuery(id+"F0.wireOp",EDGE,"E3.left")])]});
            var Q149;
            Q149=makeQuery(id+"F1.opExtrude","SWEPT_EDGE",EDGE,{"disambiguationData":[OSD([sQuery(id+"F0.wireOp",EDGE,"E0.bottom"),sQuery(id+"F0.wireOp",EDGE,"E0.left")])]});
            var Q150;
            Q150=makeQuery(id+"F1.opExtrude","SWEPT_EDGE",EDGE,{"disambiguationData":[OSD([sQuery(id+"F0.wireOp",EDGE,"E1.bottom"),sQuery(id+"F0.wireOp",EDGE,"E1.right")])]});
            var Q151;
            Q151=makeQuery(id+"F1.opExtrude","SWEPT_EDGE",EDGE,{"disambiguationData":[OSD([sQuery(id+"F0.wireOp",EDGE,"E3.top"),sQuery(id+"F0.wireOp",EDGE,"E3.right")])]});
            var Q152;
            Q152=makeQuery(id+"F1.opExtrude","SWEPT_EDGE",EDGE,{"disambiguationData":[OSD([sQuery(id+"F0.wireOp",EDGE,"E1.top"),sQuery(id+"F0.wireOp",EDGE,"E1.left")])]});
            var Q153;
            Q153=makeQuery(id+"F1.opExtrude","SWEPT_EDGE",EDGE,{"disambiguationData":[OSD([sQuery(id+"F0.wireOp",EDGE,"E3.bottom"),sQuery(id+"F0.wireOp",EDGE,"E3.right")])]});
            var Q154;
            Q154=makeQuery(id+"F1.opExtrude","CAP_EDGE",EDGE,{"disambiguationData":[OSD([sQuery(id+"F0.wireOp",EDGE,"E0.left")])],"isStart":true});
            var Q155;
            Q155=makeQuery(id+"F1.opExtrude","SWEPT_EDGE",EDGE,{"disambiguationData":[OSD([sQuery(id+"F0.wireOp",EDGE,"E0.top"),sQuery(id+"F0.wireOp",EDGE,"E0.right")])]});
            var Q156;
            Q156=makeQuery(id+"F1.opExtrude","CAP_EDGE",EDGE,{"disambiguationData":[OSD([sQuery(id+"F0.wireOp",EDGE,"E0.right")])],"isStart":false});
            var Q157;
            Q157=makeQuery(id+"F1.opExtrude","SWEPT_FACE",FACE,{"disambiguationData":[OSD([sQuery(id+"F0.wireOp",EDGE,"E0.right")])]});
            fillet(context, id + "F5", {"entities" : qUnion([Q0, Q1, Q2, Q3, Q4, Q5, Q6, Q7, Q8, Q9, Q10, Q11, Q12, Q13, Q14, Q15, Q16, Q17, Q18, Q19, Q20, Q21, Q22, Q23, Q24, Q25, Q26, Q27, Q28, Q29, Q30, Q31, Q32, Q33, Q34, Q35, Q36, Q37, Q38, Q39, Q40, Q41, Q42, Q43, Q44, Q45, Q46, Q47, Q48, Q49, Q50, Q51, Q52, Q53, Q54, Q55, Q56, Q57, Q58, Q59, Q60, Q61, Q62, Q63, Q64, Q65, Q66, Q67, Q68, Q69, Q70, Q71, Q72, Q73, Q74, Q75, Q76, Q77, Q78, Q79, Q80, Q81, Q82, Q83, Q84, Q85, Q86, Q87, Q88, Q89, Q90, Q91, Q92, Q93, Q94, Q95, Q96, Q97, Q98, Q99, Q100, Q101, Q102, Q103, Q104, Q105, Q106, Q107, Q108, Q109, Q110, Q111, Q112, Q113, Q114, Q115, Q116, Q117, Q118, Q119, Q120, Q121, Q122, Q123, Q124, Q125, Q126, Q127, Q128, Q129, Q130, Q131, Q132, Q133, Q134, Q135, Q136, Q137, Q138, Q139, Q140, Q141, Q142, Q143, Q144, Q145, Q146, Q147, Q148, Q149, Q150, Q151, Q152, Q153, Q154, Q155, Q156, Q157]), "radius" : 1 * mm, "tangentPropagation" : true, "allowEdgeOverflow" : false});
        }
    });
